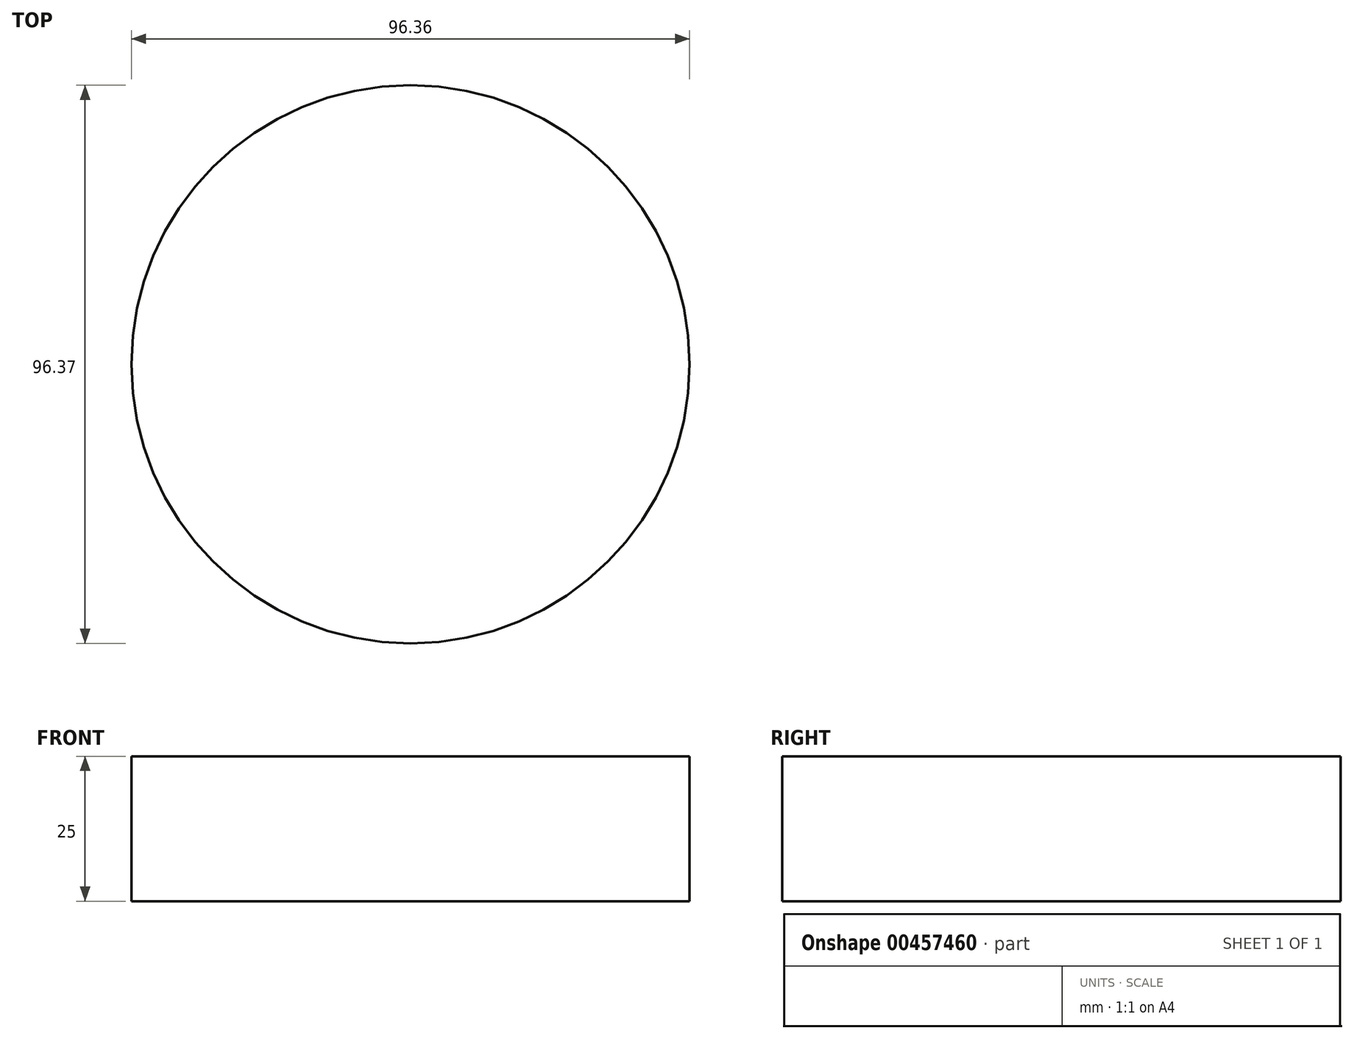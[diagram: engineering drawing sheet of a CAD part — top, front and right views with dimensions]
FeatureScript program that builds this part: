
annotation { "Feature Type Name" : "Feature", "Feature Type Description" : "" }
export const myFeature = defineFeature(function(context is Context, id is Id, definition is map)
    precondition{}
    {
        {
            var Q0;
            Q0=qCreatedBy(makeId("Top.planeOp"),FACE);
            var sketch = newSketch(context, id + "F0", { "sketchPlane" : qUnion([Q0])});
            skCircle(sketch, "E0", {"center": v(39.6, 29.27) * mm, "radius": 32.87 * mm});
            skCircle(sketch, "E1", {"center": v(45.1, 18.18) * mm, "radius": 48.18 * mm});
            skSolve(sketch);
        }
        {
            var Q0;
            Q0=sQuery(id+"F0.wireOp",EDGE,"E1");
            extrude(context, id + "F1", {"bodyType" : ToolBodyType.SURFACE, "surfaceEntities" : qUnion([Q0]), "depth" : 25 * mm});
        }
    });
